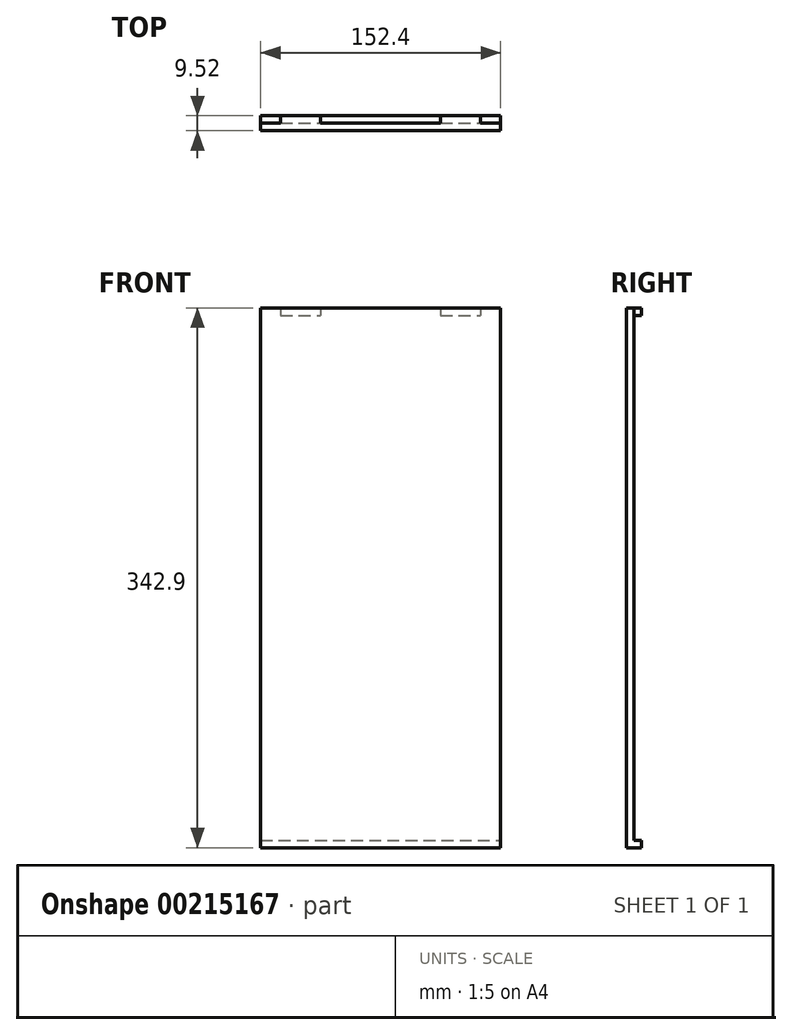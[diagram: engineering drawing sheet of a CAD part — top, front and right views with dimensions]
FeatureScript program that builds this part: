
annotation { "Feature Type Name" : "Feature", "Feature Type Description" : "" }
export const myFeature = defineFeature(function(context is Context, id is Id, definition is map)
    precondition{}
    {
        {
            var Q0;
            Q0=qCreatedBy(makeId("Front.planeOp"),FACE);
            var sketch = newSketch(context, id + "F0", { "sketchPlane" : qUnion([Q0])});
            skLineSegment(sketch, "E0.bottom", {"start": v(76.2, -171.45) * mm, "end": v(-76.2, -171.45) * mm});
            skLineSegment(sketch, "E0.top", {"start": v(76.2, 171.45) * mm, "end": v(-76.2, 171.45) * mm});
            skLineSegment(sketch, "E0.left", {"start": v(76.2, -171.45) * mm, "end": v(76.2, 171.45) * mm});
            skLineSegment(sketch, "E0.right", {"start": v(-76.2, -171.45) * mm, "end": v(-76.2, 171.45) * mm});
            skPoint(sketch, "E0.middle", {"position": v(0, 0) * mm});
            skSolve(sketch);
        }
        {
            var Q0;
            Q0 = qSketchRegion(id + "F0", true);
            extrude(context, id + "F1", {"entities" : qUnion([Q0]), "depth" : 4.76 * mm});
        }
        {
            var Q0;
            Q0=makeQuery(id+"F1.opExtrude","CAP_FACE",FACE,{"disambiguationData":[OSD([sQuery(id+"F0.wireOp",EDGE,"E0.bottom"),sQuery(id+"F0.wireOp",EDGE,"E0.top"),sQuery(id+"F0.wireOp",EDGE,"E0.left"),sQuery(id+"F0.wireOp",EDGE,"E0.right")])],"isStart":false});
            var sketch = newSketch(context, id + "F2", { "sketchPlane" : qUnion([Q0])});
            skLineSegment(sketch, "E1.bottom", {"start": v(-63.5, 171.45) * mm, "end": v(-38.1, 171.45) * mm});
            skLineSegment(sketch, "E1.top", {"start": v(-63.5, 166.69) * mm, "end": v(-38.1, 166.69) * mm});
            skLineSegment(sketch, "E1.left", {"start": v(-63.5, 171.45) * mm, "end": v(-63.5, 166.69) * mm});
            skLineSegment(sketch, "E1.right", {"start": v(-38.1, 171.45) * mm, "end": v(-38.1, 166.69) * mm});
            skLineSegment(sketch, "E2.bottom", {"start": v(38.1, 171.45) * mm, "end": v(63.5, 171.45) * mm});
            skLineSegment(sketch, "E2.top", {"start": v(38.1, 166.69) * mm, "end": v(63.5, 166.69) * mm});
            skLineSegment(sketch, "E2.left", {"start": v(38.1, 171.45) * mm, "end": v(38.1, 166.69) * mm});
            skLineSegment(sketch, "E2.right", {"start": v(63.5, 171.45) * mm, "end": v(63.5, 166.69) * mm});
            skSolve(sketch);
        }
        {
            var Q0;
            Q0 = qSketchRegion(id + "F2", true);
            extrude(context, id + "F3", {"entities" : qUnion([Q0]), "operationType" : NewBodyOperationType.ADD, "oppositeDirection" : true, "depth" : 9.52 * mm});
        }
        {
            var Q0;
            Q0=makeQuery(id+"F1.opExtrude","CAP_FACE",FACE,{"disambiguationData":[OSD([sQuery(id+"F0.wireOp",EDGE,"E0.bottom"),sQuery(id+"F0.wireOp",EDGE,"E0.top"),sQuery(id+"F0.wireOp",EDGE,"E0.left"),sQuery(id+"F0.wireOp",EDGE,"E0.right")])],"isStart":false});
            var sketch = newSketch(context, id + "F4", { "sketchPlane" : qUnion([Q0])});
            skLineSegment(sketch, "E3.bottom", {"start": v(-76.2, -171.45) * mm, "end": v(76.2, -171.45) * mm});
            skLineSegment(sketch, "E3.top", {"start": v(-76.2, -166.69) * mm, "end": v(76.2, -166.69) * mm});
            skLineSegment(sketch, "E3.left", {"start": v(-76.2, -171.45) * mm, "end": v(-76.2, -166.69) * mm});
            skLineSegment(sketch, "E3.right", {"start": v(76.2, -171.45) * mm, "end": v(76.2, -166.69) * mm});
            skSolve(sketch);
        }
        {
            var Q0;
            Q0 = qSketchRegion(id + "F4", true);
            extrude(context, id + "F5", {"entities" : qUnion([Q0]), "operationType" : NewBodyOperationType.ADD, "oppositeDirection" : true, "depth" : 9.52 * mm});
        }
    });
